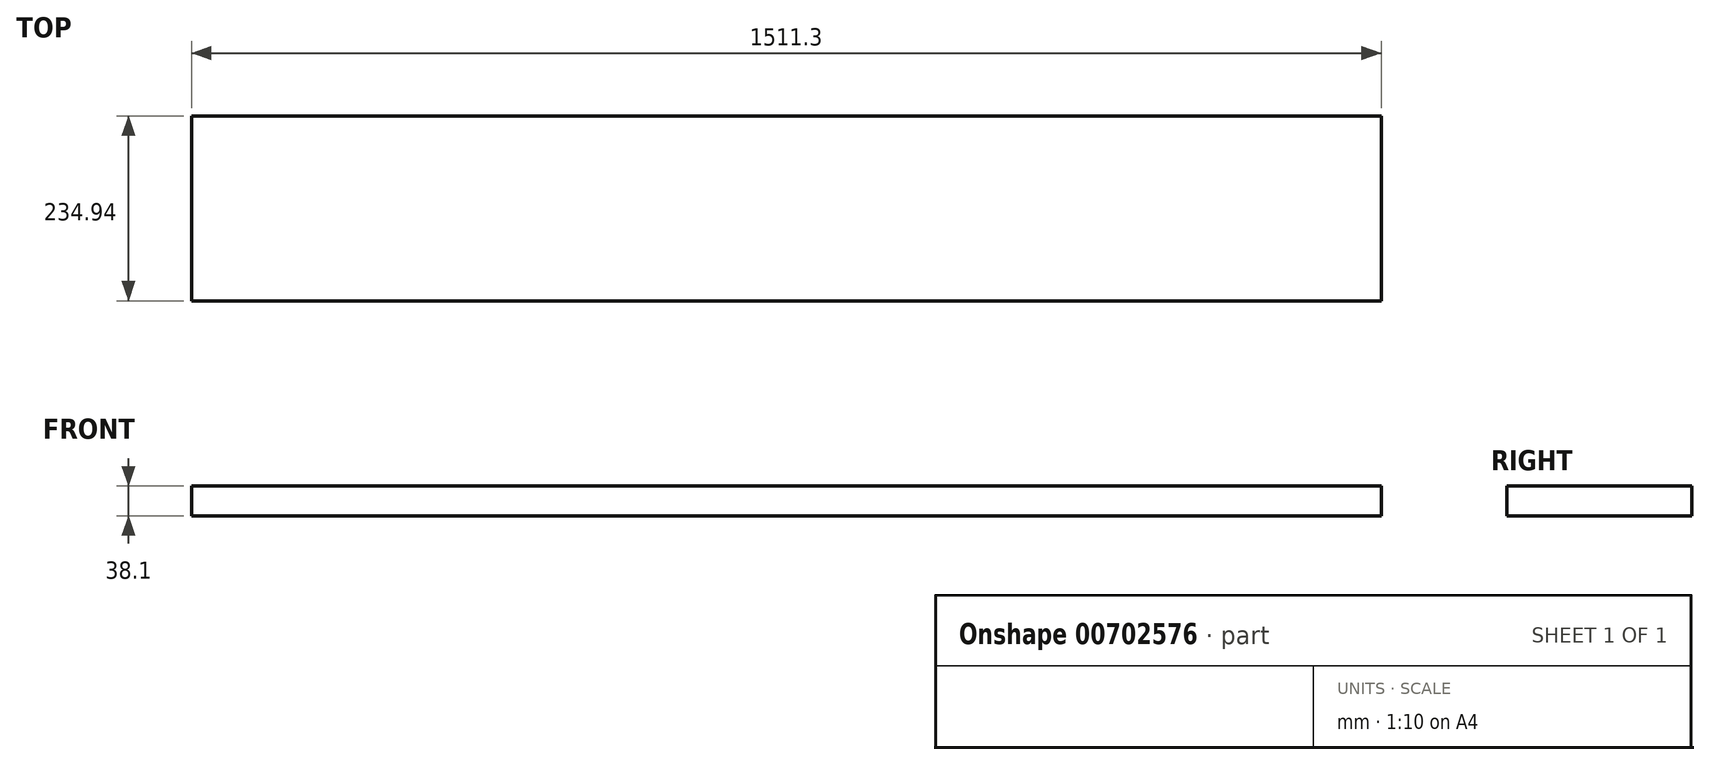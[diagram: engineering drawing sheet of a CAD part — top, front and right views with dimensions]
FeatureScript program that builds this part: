
annotation { "Feature Type Name" : "Feature", "Feature Type Description" : "" }
export const myFeature = defineFeature(function(context is Context, id is Id, definition is map)
    precondition{}
    {
        {
            var Q0;
            Q0=qCreatedBy(makeId("Top.planeOp"),FACE);
            var sketch = newSketch(context, id + "F0", { "sketchPlane" : qUnion([Q0])});
            skLineSegment(sketch, "E0.bottom", {"start": v(755.65, 117.48) * mm, "end": v(-755.65, 117.48) * mm});
            skLineSegment(sketch, "E0.top", {"start": v(755.65, -117.48) * mm, "end": v(-755.65, -117.48) * mm});
            skLineSegment(sketch, "E0.left", {"start": v(755.65, 117.48) * mm, "end": v(755.65, -117.48) * mm});
            skLineSegment(sketch, "E0.right", {"start": v(-755.65, 117.48) * mm, "end": v(-755.65, -117.48) * mm});
            skPoint(sketch, "E0.middle", {"position": v(0, 0) * mm});
            skSolve(sketch);
        }
        {
            var Q0;
            Q0 = qSketchRegion(id + "F0", true);
            extrude(context, id + "F1", {"entities" : qUnion([Q0]), "depth" : 38.1 * mm, "offsetDistance" : 25.4 * mm});
        }
    });
